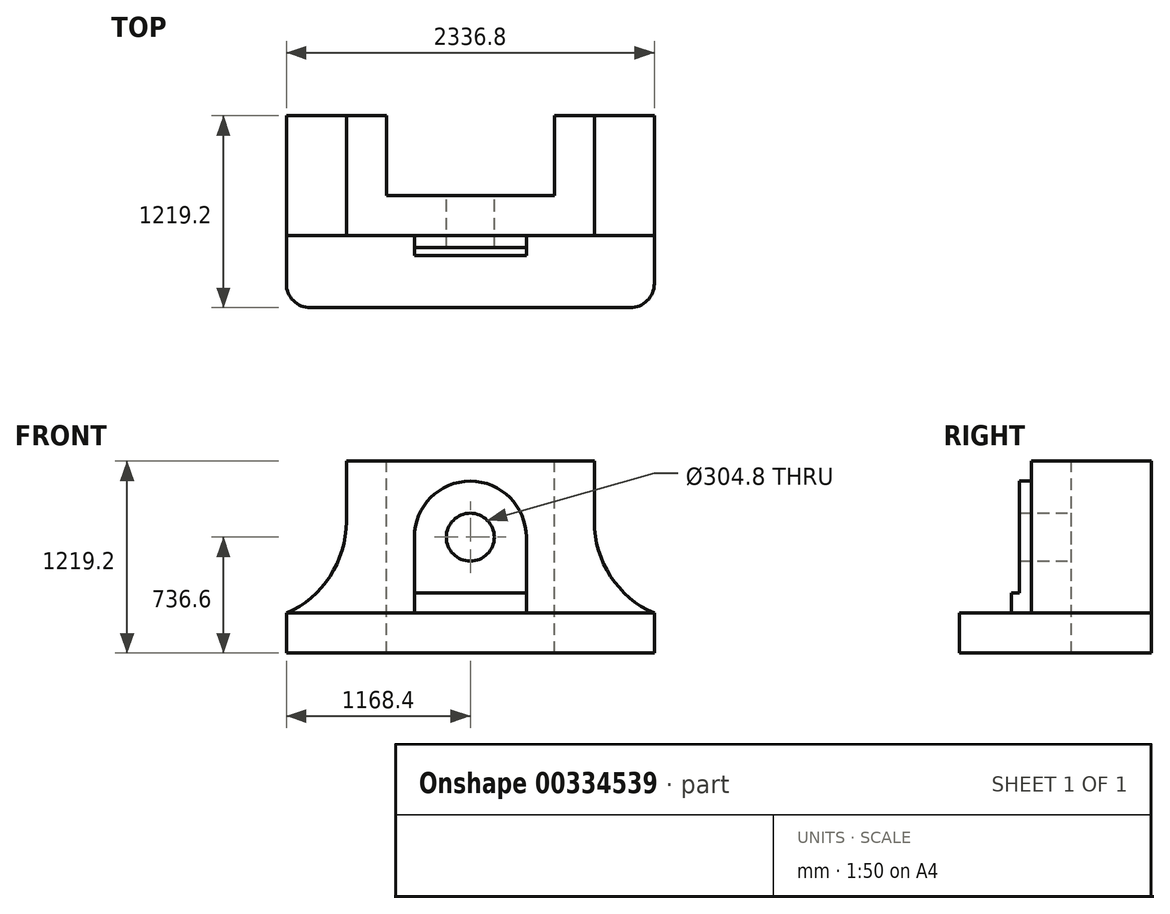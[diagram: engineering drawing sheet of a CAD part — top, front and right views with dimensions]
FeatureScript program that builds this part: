
annotation { "Feature Type Name" : "Feature", "Feature Type Description" : "" }
export const myFeature = defineFeature(function(context is Context, id is Id, definition is map)
    precondition{}
    {
        {
            var Q0;
            Q0=qCreatedBy(makeId("Top.planeOp"),FACE);
            var sketch = newSketch(context, id + "F0", { "sketchPlane" : qUnion([Q0])});
            skSolve(sketch);
        }
        {
            var Q0;
            Q0=qCreatedBy(makeId("Front.planeOp"),FACE);
            var sketch = newSketch(context, id + "F1", { "sketchPlane" : qUnion([Q0])});
            skLineSegment(sketch, "E0", {"start": v(0, 0) * mm, "end": v(1168.4, 0) * mm});
            skLineSegment(sketch, "E1", {"start": v(1168.4, 0) * mm, "end": v(1168.4, 254) * mm});
            skLineSegment(sketch, "E2", {"start": v(0, 1219.2) * mm, "end": v(787.4, 1219.2) * mm});
            skLineSegment(sketch, "E3", {"start": v(787.4, 1219.2) * mm, "end": v(787.4, 835.99) * mm});
            skCircle(sketch, "E4", {"center": v(1422.4, 835.99) * mm, "radius": 635 * mm});
            skPoint(sketch, "E4.third.point", {"position": v(1966.8, 1162.87) * mm});
            skLineSegment(sketch, "E5", {"start": v(1168.4, 254) * mm, "end": v(0, 254) * mm});
            skLineSegment(sketch, "E6.MirrorCS", {"start": v(0, 0) * mm, "end": v(-1168.4, 0) * mm});
            skLineSegment(sketch, "E7.MirrorCS", {"start": v(-1168.4, 0) * mm, "end": v(-1168.4, 254) * mm});
            skLineSegment(sketch, "E8.MirrorCS", {"start": v(-1168.4, 254) * mm, "end": v(0, 254) * mm});
            skLineSegment(sketch, "E9.MirrorCS", {"start": v(0, 1219.2) * mm, "end": v(-787.4, 1219.2) * mm});
            skLineSegment(sketch, "E10.MirrorCS", {"start": v(-787.4, 1219.2) * mm, "end": v(-787.4, 835.99) * mm});
            skCircle(sketch, "E11.MirrorC", {"center": v(-1422.4, 835.99) * mm, "radius": 635 * mm});
            skCircle(sketch, "E12", {"center": v(0, 736.6) * mm, "radius": 355.6 * mm});
            skLineSegment(sketch, "E13", {"start": v(-355.6, 736.6) * mm, "end": v(-355.6, 254) * mm});
            skLineSegment(sketch, "E14", {"start": v(355.6, 736.6) * mm, "end": v(355.6, 254) * mm});
            skCircle(sketch, "E15", {"center": v(0, 736.6) * mm, "radius": 152.4 * mm});
            skLineSegment(sketch, "E16", {"start": v(-355.6, 381) * mm, "end": v(355.6, 381) * mm});
            skSolve(sketch);
        }
        {
            var Q0;
            Q0=makeQuery(id+"F1.imprint","IMPRINT",FACE,{"disambiguationData":[TD([[makeQuery(id+"F1.imprint","IMPRINT",EDGE,{"derivedFrom":sQuery(id+"F1.wireOp",EDGE,"E2")}),-1.0]])]});
            extrude(context, id + "F2", {"entities" : qUnion([Q0]), "depth" : 762 * mm});
        }
        {
            var Q0;
            Q0 = qSketchRegion(id + "F0", true);
            var Q1;
            Q1=makeQuery(id+"F1.imprint","IMPRINT",FACE,{"disambiguationData":[TD([[makeQuery(id+"F1.imprint","IMPRINT",EDGE,{"derivedFrom":sQuery(id+"F1.wireOp",EDGE,"E0")}),1.0]])]});
            extrude(context, id + "F3", {"entities" : qUnion([Q0, Q1]), "operationType" : NewBodyOperationType.ADD, "depth" : 1219.2 * mm});
        }
        {
            var Q0;
            Q0=makeQuery(id+"F1.imprint","IMPRINT",FACE,{"disambiguationData":[TD([[makeQuery(id+"F1.imprint","IMPRINT",EDGE,{"derivedFrom":sQuery(id+"F1.wireOp",EDGE,"E15")}),-1.0]])]});
            var Q1;
            {var subQ0=sQuery(id+"F1.wireOp",EDGE,"E13");var subQ1=sQuery(id+"F1.wireOp",EDGE,"E12");var subQ2=makeQuery(id+"F1.imprint","INTERSECT",VERTEX,{"derivedFrom":[subQ1,subQ0]});Q1=makeQuery(id+"F1.imprint","IMPRINT",FACE,{"disambiguationData":[TD([[makeQuery(id+"F1.imprint","IMPRINT",EDGE,{"disambiguationData":[TD([[subQ2,-1.0]])],"derivedFrom":subQ1}),-1.0]])]});}
            var Q2;
            {var subQ0=sQuery(id+"F1.wireOp",EDGE,"E14");var subQ1=sQuery(id+"F1.wireOp",EDGE,"E12");var subQ2=makeQuery(id+"F1.imprint","INTERSECT",VERTEX,{"derivedFrom":[subQ1,subQ0]});Q2=makeQuery(id+"F1.imprint","IMPRINT",FACE,{"disambiguationData":[TD([[makeQuery(id+"F1.imprint","IMPRINT",EDGE,{"disambiguationData":[TD([[subQ2,1.0]])],"derivedFrom":subQ1}),-1.0]])]});}
            extrude(context, id + "F4", {"entities" : qUnion([Q0, Q1, Q2]), "operationType" : NewBodyOperationType.ADD, "depth" : 838.2 * mm});
        }
        {
            var Q0;
            {var subQ1=sQuery(id+"F1.wireOp",EDGE,"E8.MirrorCS");var subQ5=sQuery(id+"F1.wireOp",EDGE,"E5");var subQ6=makeQuery(id+"F1.imprint","INTERSECT",VERTEX,{"derivedFrom":[subQ5,subQ1]});Q0=makeQuery(id+"F1.imprint","IMPRINT",FACE,{"disambiguationData":[TD([[makeQuery(id+"F1.imprint","IMPRINT",EDGE,{"disambiguationData":[TD([[subQ6,1.0]])],"derivedFrom":subQ5}),-1.0]])]});}
            extrude(context, id + "F5", {"entities" : qUnion([Q0]), "operationType" : NewBodyOperationType.ADD, "depth" : 889 * mm});
        }
        {
            var Q0;
            Q0=makeQuery(id+"F2.opExtrude","SWEPT_FACE",FACE,{"disambiguationData":[OSD([sQuery(id+"F1.wireOp",EDGE,"E2"),sQuery(id+"F1.wireOp",EDGE,"E9.MirrorCS")])]});
            var sketch = newSketch(context, id + "F6", { "sketchPlane" : qUnion([Q0])});
            skLineSegment(sketch, "E17.bottom", {"start": v(-533.4, 0) * mm, "end": v(533.4, 0) * mm});
            skLineSegment(sketch, "E17.top", {"start": v(-533.4, -508) * mm, "end": v(533.4, -508) * mm});
            skLineSegment(sketch, "E17.left", {"start": v(-533.4, 0) * mm, "end": v(-533.4, -508) * mm});
            skLineSegment(sketch, "E17.right", {"start": v(533.4, 0) * mm, "end": v(533.4, -508) * mm});
            skSolve(sketch);
        }
        {
            var Q0;
            Q0=makeQuery(id+"F6.imprint","IMPRINT",FACE,{"disambiguationData":[TD([[makeQuery(id+"F6.imprint","IMPRINT",EDGE,{"derivedFrom":sQuery(id+"F6.wireOp",EDGE,"E17.bottom")}),-1.0]])]});
            extrude(context, id + "F7", {"entities" : qUnion([Q0]), "operationType" : NewBodyOperationType.REMOVE, "oppositeDirection" : true, "depth" : 2270.76 * mm});
        }
        {
            var Q0;
            Q0=makeQuery(id+"F3.opExtrude","CAP_EDGE",EDGE,{"disambiguationData":[OSD([sQuery(id+"F1.wireOp",EDGE,"E1")])],"isStart":false});
            var Q1;
            Q1=makeQuery(id+"F3.opExtrude","CAP_EDGE",EDGE,{"disambiguationData":[OSD([sQuery(id+"F1.wireOp",EDGE,"E7.MirrorCS")])],"isStart":false});
            fillet(context, id + "F8", {"entities" : qUnion([Q0, Q1]), "radius" : 152.4 * mm, "tangentPropagation" : true, "allowEdgeOverflow" : false});
        }
    });
